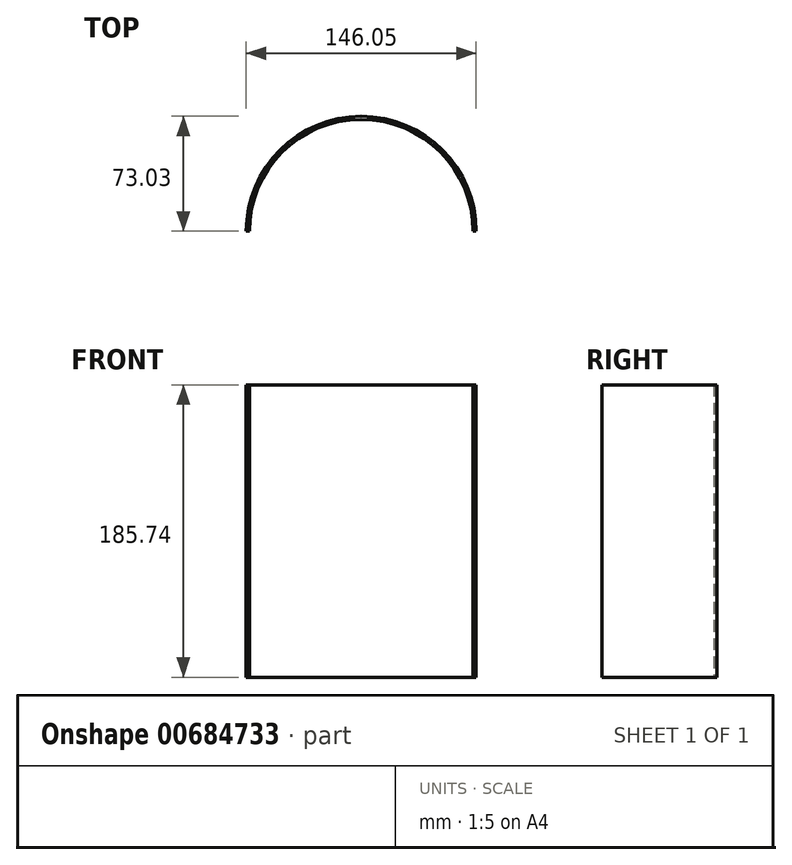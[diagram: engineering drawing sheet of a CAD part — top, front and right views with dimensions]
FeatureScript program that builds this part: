
annotation { "Feature Type Name" : "Feature", "Feature Type Description" : "" }
export const myFeature = defineFeature(function(context is Context, id is Id, definition is map)
    precondition{}
    {
        {
            var Q0;
            Q0=qCreatedBy(makeId("Top.planeOp"),FACE);
            var sketch = newSketch(context, id + "F0", { "sketchPlane" : qUnion([Q0])});
            skLineSegment(sketch, "E0", {"start": v(0, 0) * mm, "end": v(-146.05, 0) * mm});
            skArc(sketch, "E1", {"start": v(0, 0) * mm, "mid": v(-73.03, 73.03) * mm, "end": v(-146.05, 0) * mm});
            skArc(sketch, "E2", {"start": v(-2, 0) * mm, "mid": v(-73.03, 71.03) * mm, "end": v(-144.05, 0) * mm});
            skSolve(sketch);
        }
        {
            var Q0;
            {var subQ0=sQuery(id+"F0.wireOp",EDGE,"E1");Q0=makeQuery(id+"F0.imprint","IMPRINT",FACE,{"disambiguationData":[TD([[makeQuery(id+"F0.imprint","IMPRINT",EDGE,{"derivedFrom":subQ0}),1.0]])]});}
            extrude(context, id + "F1", {"entities" : qUnion([Q0]), "depth" : 185.74 * mm, "offsetDistance" : 25.4 * mm});
        }
    });
